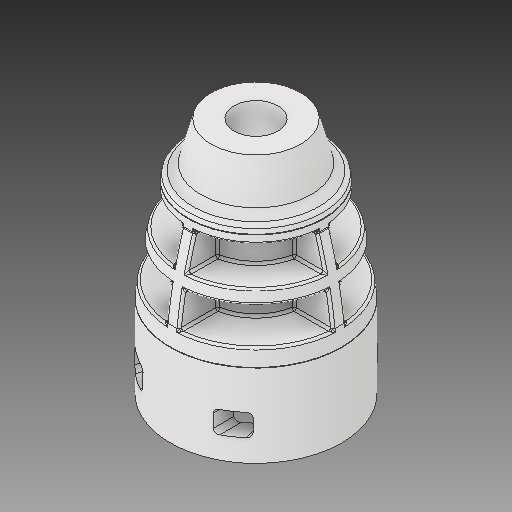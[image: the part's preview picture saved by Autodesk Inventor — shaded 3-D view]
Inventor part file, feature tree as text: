
AUTODESK INVENTOR PART (.ipt)
format: ipt  version: 2018 (Build 220112000, 112)  size: 834,560 bytes
history: native  units: in
note: dims shown in document units (in); Inventor stores cm internally (conversion verified against a paired STEP export)
features: fillet x1
ambient origin geometry x8: Origin, YZ Plane, XZ Plane, XY Plane, X Axis, Y Axis, Z Axis, Center Point
bodies: Solid1 (feature_tree)
feature tree (1):
  fillet  "Fillet3"  [1 undecoded]
note: 1 required parameter value undecoded (feature->parameter linkage not recoverable at this tier; creation-order binding heuristic only, values carry confidence <= 0.55)
